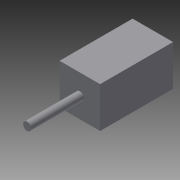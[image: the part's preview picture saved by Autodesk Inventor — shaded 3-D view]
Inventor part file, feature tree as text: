
AUTODESK INVENTOR PART (.ipt)
format: ipt  version: 2013 (Build 170138000, 138)  size: 76,288 bytes
history: native  units: in
note: dims shown in document units (in); Inventor stores cm internally (conversion verified against a paired STEP export)
features: extrude x2, sketch x2
ambient origin geometry x8: Origin, YZ Plane, XZ Plane, XY Plane, X Axis, Y Axis, Z Axis, Center Point
bodies: Solid1 (feature_tree)
feature tree (4):
  extrude  "Extrusion1"  Depth=2.5in
  extrude  "Extrusion2"  Depth=0.5in
  sketch  "Sketch1"  dims[d0=2.5in d1=2.5in]
  sketch  "Sketch2"  dims[d2=4.504in d3=0.0in d4=0.5in d5=3.25in d6=0.0in]
